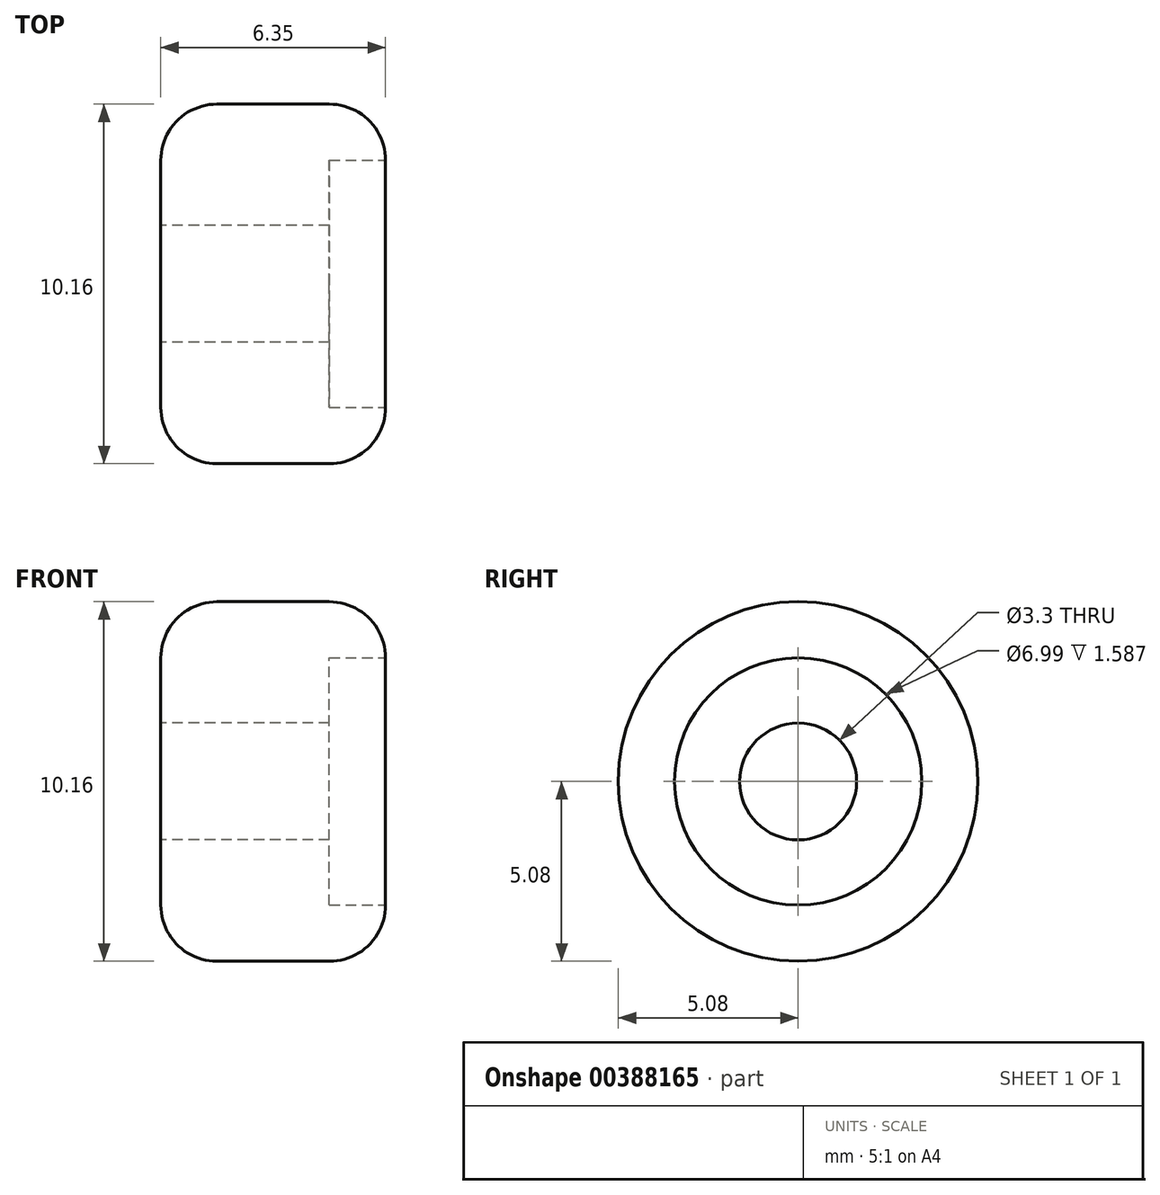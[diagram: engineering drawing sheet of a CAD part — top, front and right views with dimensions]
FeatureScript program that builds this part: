
annotation { "Feature Type Name" : "Feature", "Feature Type Description" : "" }
export const myFeature = defineFeature(function(context is Context, id is Id, definition is map)
    precondition{}
    {
        {
            var Q0;
            Q0=qCreatedBy(makeId("Right.planeOp"),FACE);
            var sketch = newSketch(context, id + "F0", { "sketchPlane" : qUnion([Q0])});
            skCircle(sketch, "E0", {"center": v(0, 0) * mm, "radius": 5.08 * mm});
            skCircle(sketch, "E1", {"center": v(0, 0) * mm, "radius": 1.65 * mm});
            skSolve(sketch);
        }
        {
            var Q0;
            Q0=qSketchRegion(id+"F0",true);
            extrude(context, id + "F1", {"entities" : qUnion([Q0]), "depth" : 6.35 * mm});
        }
        {
            var Q0;
            Q0=makeQuery(id+"F1.opExtrude","CAP_EDGE",EDGE,{"disambiguationData":[OSD([sQuery(id+"F0.wireOp",EDGE,"E0")])],"isStart":false});
            var Q1;
            Q1=makeQuery(id+"F1.opExtrude","CAP_EDGE",EDGE,{"disambiguationData":[OSD([sQuery(id+"F0.wireOp",EDGE,"E0")])],"isStart":true});
            fillet(context, id + "F2", {"entities" : qUnion([Q0, Q1]), "radius" : 1.59 * mm, "tangentPropagation" : true, "allowEdgeOverflow" : false});
        }
        {
            var Q0;
            Q0=makeQuery(id+"F1.opExtrude","CAP_FACE",FACE,{"disambiguationData":[OSD([sQuery(id+"F0.wireOp",EDGE,"E0"),sQuery(id+"F0.wireOp",EDGE,"E1")])],"isStart":false});
            var sketch = newSketch(context, id + "F3", { "sketchPlane" : qUnion([Q0])});
            skCircle(sketch, "E2", {"center": v(0, 0) * mm, "radius": 1.65 * mm});
            skCircle(sketch, "E3", {"center": v(0, 0) * mm, "radius": 3.5 * mm});
            skSolve(sketch);
        }
        {
            var Q0;
            Q0=qSketchRegion(id+"F3",true);
            extrude(context, id + "F4", {"entities" : qUnion([Q0]), "operationType" : NewBodyOperationType.REMOVE, "oppositeDirection" : true, "depth" : 1.59 * mm});
        }
    });
